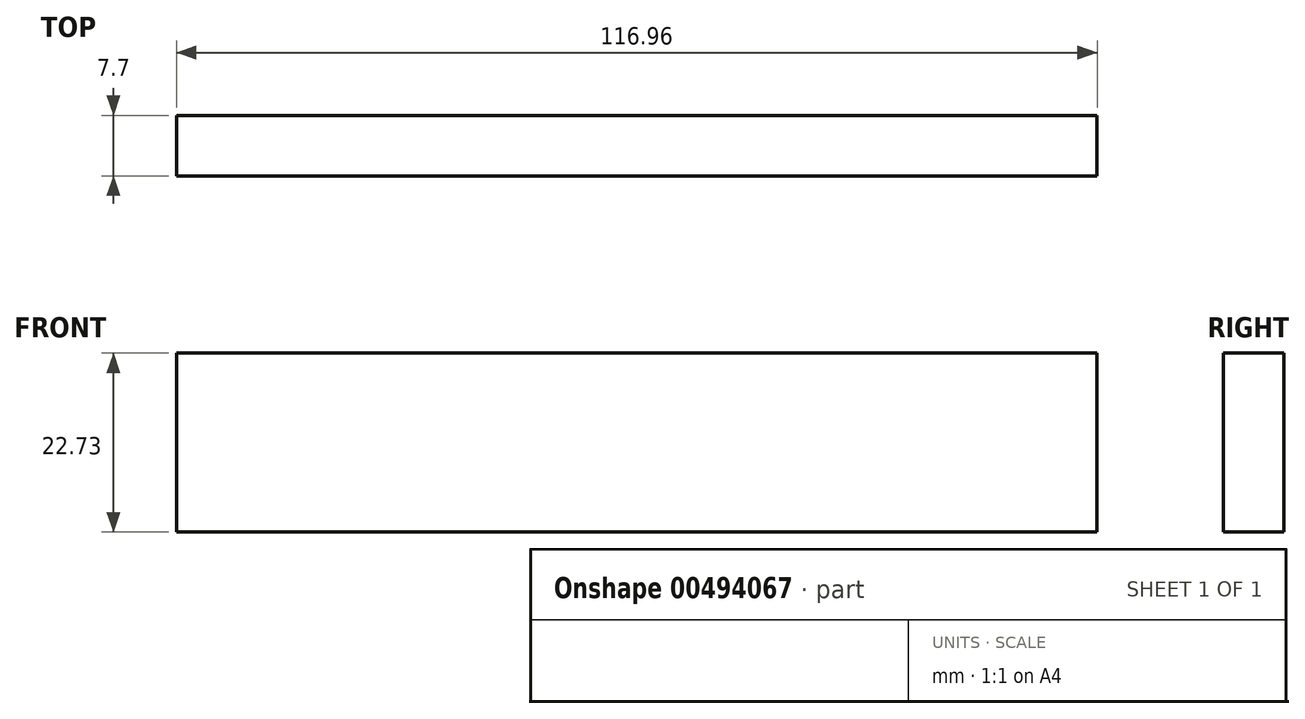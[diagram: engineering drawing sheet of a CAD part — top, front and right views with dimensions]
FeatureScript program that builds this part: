
annotation { "Feature Type Name" : "Feature", "Feature Type Description" : "" }
export const myFeature = defineFeature(function(context is Context, id is Id, definition is map)
    precondition{}
    {
        {
            var Q0;
            Q0=qCreatedBy(makeId("Front.planeOp"),FACE);
            var sketch = newSketch(context, id + "F0", { "sketchPlane" : qUnion([Q0])});
            skLineSegment(sketch, "E0.bottom", {"start": v(-60.37, 6.67) * mm, "end": v(56.59, 6.67) * mm});
            skLineSegment(sketch, "E0.top", {"start": v(-60.37, -16.06) * mm, "end": v(56.59, -16.06) * mm});
            skLineSegment(sketch, "E0.left", {"start": v(-60.37, 6.67) * mm, "end": v(-60.37, -16.06) * mm});
            skLineSegment(sketch, "E0.right", {"start": v(56.59, 6.67) * mm, "end": v(56.59, -16.06) * mm});
            skSolve(sketch);
        }
        {
            var Q0;
            Q0=makeQuery(id+"F0.imprint","IMPRINT",FACE,{"disambiguationData":[TD([[makeQuery(id+"F0.imprint","IMPRINT",EDGE,{"derivedFrom":sQuery(id+"F0.wireOp",EDGE,"E0.bottom")}),-1.0]])]});
            extrude(context, id + "F1", {"entities" : qUnion([Q0]), "depth" : 7.7 * mm});
        }
    });
